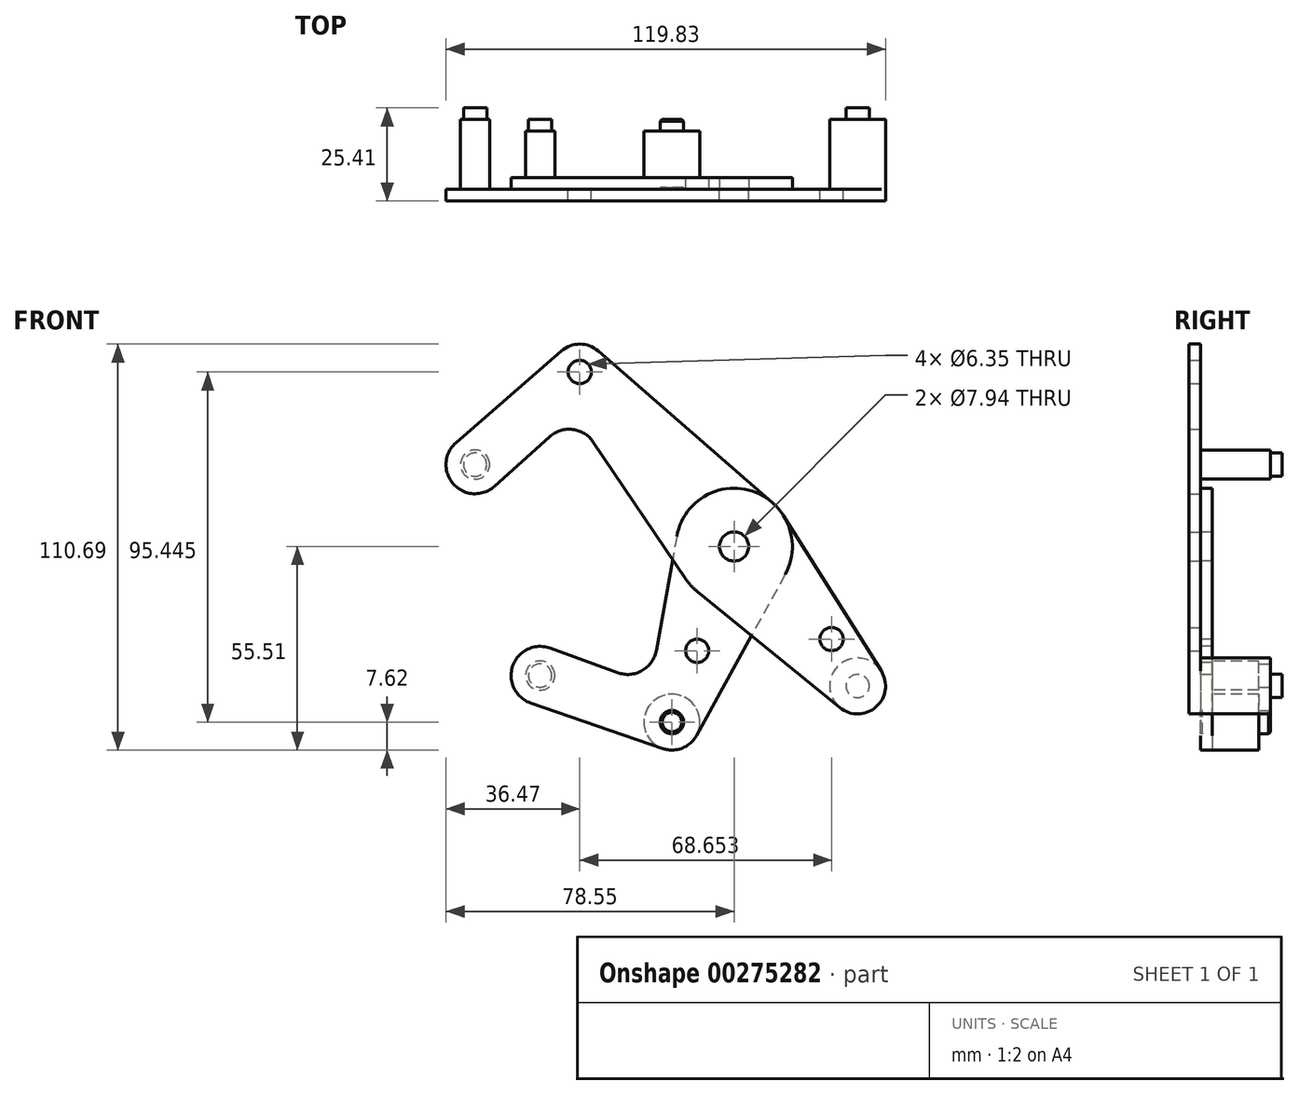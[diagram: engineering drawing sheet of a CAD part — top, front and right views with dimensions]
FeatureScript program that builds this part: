
annotation { "Feature Type Name" : "Feature", "Feature Type Description" : "" }
export const myFeature = defineFeature(function(context is Context, id is Id, definition is map)
    precondition{}
    {
        {
            var Q0;
            Q0=qCreatedBy(makeId("Front.planeOp"),FACE);
            var sketch = newSketch(context, id + "F0", { "sketchPlane" : qUnion([Q0])});
            skLineSegment(sketch, "E0", {"start": v(-42.08, 47.56) * mm, "end": v(42.08, -47.56) * mm, "construction": true});
            skCircle(sketch, "E1", {"center": v(0, 0) * mm, "radius": 3.18 * mm});
            skCircle(sketch, "E2", {"center": v(33.66, -38.04) * mm, "radius": 3.18 * mm});
            skCircle(sketch, "E3", {"center": v(-42.08, 47.56) * mm, "radius": 3.18 * mm});
            skCircle(sketch, "E4", {"center": v(-70.61, 22.3) * mm, "radius": 3.18 * mm});
            skLineSegment(sketch, "E5", {"start": v(-42.08, 47.56) * mm, "end": v(-70.61, 22.3) * mm, "construction": true});
            skCircle(sketch, "E6", {"center": v(33.66, -38.04) * mm, "radius": 7.62 * mm});
            skCircle(sketch, "E7", {"center": v(-70.61, 22.3) * mm, "radius": 7.94 * mm});
            skCircle(sketch, "E8", {"center": v(-42.08, 47.56) * mm, "radius": 7.62 * mm});
            skLineSegment(sketch, "E9", {"start": v(-75.82, 28.3) * mm, "end": v(-47.08, 53.3) * mm});
            skLineSegment(sketch, "E10", {"start": v(-65.3, 16.4) * mm, "end": v(-50.27, 29.93) * mm});
            skCircle(sketch, "E11", {"center": v(0, 0) * mm, "radius": 15.88 * mm});
            skLineSegment(sketch, "E12", {"start": v(-37.08, 53.3) * mm, "end": v(10.42, 11.98) * mm});
            skLineSegment(sketch, "E13", {"start": v(-38.39, 28.47) * mm, "end": v(-13.16, -8.89) * mm});
            skLineSegment(sketch, "E14", {"start": v(-10.02, -12.31) * mm, "end": v(28.85, -43.95) * mm});
            skLineSegment(sketch, "E15", {"start": v(13.44, 8.45) * mm, "end": v(40.12, -33.99) * mm});
            skArc(sketch, "E16.filletArc", {"start": v(-38.39, 28.47) * mm, "mid": v(-44, 31.9) * mm, "end": v(-50.27, 29.93) * mm});
            skLineSegment(sketch, "E17", {"start": v(0, 0) * mm, "end": v(-16.95, -47.89) * mm, "construction": true});
            skLineSegment(sketch, "E18", {"start": v(-16.95, -47.89) * mm, "end": v(-52.86, -35.18) * mm, "construction": true});
            skCircle(sketch, "E19", {"center": v(-52.86, -35.18) * mm, "radius": 3.18 * mm});
            skCircle(sketch, "E20", {"center": v(-16.95, -47.89) * mm, "radius": 3.18 * mm});
            skCircle(sketch, "E21", {"center": v(-52.86, -35.18) * mm, "radius": 7.94 * mm});
            skCircle(sketch, "E22", {"center": v(-16.95, -47.89) * mm, "radius": 7.62 * mm});
            skLineSegment(sketch, "E23", {"start": v(-50.15, -27.72) * mm, "end": v(-31.72, -34.42) * mm});
            skLineSegment(sketch, "E24", {"start": v(-55.45, -42.68) * mm, "end": v(-19.43, -55.1) * mm});
            skLineSegment(sketch, "E25", {"start": v(-15.63, 2.8) * mm, "end": v(-21.2, -28.35) * mm});
            skLineSegment(sketch, "E26", {"start": v(13.9, -7.66) * mm, "end": v(-10.27, -51.57) * mm});
            skArc(sketch, "E27.filletArc", {"start": v(-31.72, -34.42) * mm, "mid": v(-25.05, -33.83) * mm, "end": v(-21.2, -28.35) * mm});
            skCircle(sketch, "E28", {"center": v(-10.06, -28.43) * mm, "radius": 3.18 * mm});
            skCircle(sketch, "E29", {"center": v(26.57, -25.24) * mm, "radius": 3.18 * mm});
            skLineSegment(sketch, "E30", {"start": v(26.57, -25.24) * mm, "end": v(24.2, -27.34) * mm, "construction": true});
            skCircle(sketch, "E31", {"center": v(0, 0) * mm, "radius": 3.97 * mm});
            skSolve(sketch);
        }
        {
            var Q0;
            Q0=qCreatedBy(makeId("Front.planeOp"),FACE);
            cPlane(context, id + "F1", {"entities" : qUnion([Q0]), "cplaneType" : CPlaneType.OFFSET, "offset" : 9.52 * mm, "oppositeDirection" : true, "width" : 254 * mm, "height" : 254 * mm});
        }
        {
            var Q0;
            Q0=makeQuery(id+"F0.imprint","IMPRINT",FACE,{"disambiguationData":[TD([[makeQuery(id+"F0.imprint","IMPRINT",EDGE,{"derivedFrom":sQuery(id+"F0.wireOp",EDGE,"E2")}),-1.0]])]});
            var Q1;
            Q1=makeQuery(id+"F0.imprint","IMPRINT",FACE,{"disambiguationData":[TD([[makeQuery(id+"F0.imprint","IMPRINT",EDGE,{"derivedFrom":sQuery(id+"F0.wireOp",EDGE,"E3")}),-1.0]])]});
            var Q2;
            Q2=makeQuery(id+"F0.imprint","IMPRINT",FACE,{"disambiguationData":[TD([[makeQuery(id+"F0.imprint","IMPRINT",EDGE,{"derivedFrom":sQuery(id+"F0.wireOp",EDGE,"E4")}),-1.0]])]});
            var Q3;
            {var subQ0=sQuery(id+"F0.wireOp",EDGE,"E13");var subQ1=sQuery(id+"F0.wireOp",EDGE,"E11");var subQ2=makeQuery(id+"F0.imprint","INTERSECT",VERTEX,{"derivedFrom":[subQ1,subQ0]});Q3=makeQuery(id+"F0.imprint","IMPRINT",FACE,{"disambiguationData":[TD([[makeQuery(id+"F0.imprint","IMPRINT",EDGE,{"disambiguationData":[TD([[subQ2,1.0]])],"derivedFrom":subQ1}),-1.0]])]});}
            var Q4;
            {var subQ0=sQuery(id+"F0.wireOp",EDGE,"E14");var subQ1=sQuery(id+"F0.wireOp",EDGE,"E11");var subQ2=makeQuery(id+"F0.imprint","INTERSECT",VERTEX,{"derivedFrom":[subQ1,subQ0]});Q4=makeQuery(id+"F0.imprint","IMPRINT",FACE,{"disambiguationData":[TD([[makeQuery(id+"F0.imprint","IMPRINT",EDGE,{"disambiguationData":[TD([[subQ2,-1.0]])],"derivedFrom":subQ1}),-1.0]])]});}
            var Q5;
            {var subQ0=sQuery(id+"F0.wireOp",EDGE,"E15");Q5=makeQuery(id+"F0.imprint","IMPRINT",FACE,{"disambiguationData":[TD([[makeQuery(id+"F0.imprint","IMPRINT",EDGE,{"derivedFrom":subQ0}),-1.0]])]});}
            var Q6;
            {var subQ1=sQuery(id+"F0.wireOp",EDGE,"E9");Q6=makeQuery(id+"F0.imprint","IMPRINT",FACE,{"disambiguationData":[TD([[makeQuery(id+"F0.imprint","IMPRINT",EDGE,{"derivedFrom":subQ1}),-1.0]])]});}
            var Q7;
            Q7=makeQuery(id+"F0.imprint","IMPRINT",FACE,{"disambiguationData":[TD([[makeQuery(id+"F0.imprint","IMPRINT",EDGE,{"derivedFrom":sQuery(id+"F0.wireOp",EDGE,"E31")}),-1.0]])]});
            extrude(context, id + "F2", {"entities" : qUnion([Q0, Q1, Q2, Q3, Q4, Q5, Q6, Q7]), "depth" : 3.17 * mm});
        }
        {
            var Q0;
            Q0=makeQuery(id+"F0.imprint","IMPRINT",FACE,{"disambiguationData":[TD([[makeQuery(id+"F0.imprint","IMPRINT",EDGE,{"derivedFrom":sQuery(id+"F0.wireOp",EDGE,"E19")}),-1.0]])]});
            var Q1;
            Q1=makeQuery(id+"F0.imprint","IMPRINT",FACE,{"disambiguationData":[TD([[makeQuery(id+"F0.imprint","IMPRINT",EDGE,{"derivedFrom":sQuery(id+"F0.wireOp",EDGE,"E20")}),-1.0]])]});
            var Q2;
            {var subQ0=sQuery(id+"F0.wireOp",EDGE,"E13");var subQ1=sQuery(id+"F0.wireOp",EDGE,"E11");var subQ2=makeQuery(id+"F0.imprint","INTERSECT",VERTEX,{"derivedFrom":[subQ1,subQ0]});Q2=makeQuery(id+"F0.imprint","IMPRINT",FACE,{"disambiguationData":[TD([[makeQuery(id+"F0.imprint","IMPRINT",EDGE,{"disambiguationData":[TD([[subQ2,1.0]])],"derivedFrom":subQ1}),-1.0]])]});}
            var Q3;
            {var subQ0=sQuery(id+"F0.wireOp",EDGE,"E14");var subQ1=sQuery(id+"F0.wireOp",EDGE,"E11");var subQ2=makeQuery(id+"F0.imprint","INTERSECT",VERTEX,{"derivedFrom":[subQ1,subQ0]});Q3=makeQuery(id+"F0.imprint","IMPRINT",FACE,{"disambiguationData":[TD([[makeQuery(id+"F0.imprint","IMPRINT",EDGE,{"disambiguationData":[TD([[subQ2,-1.0]])],"derivedFrom":subQ1}),-1.0]])]});}
            var Q4;
            {var subQ10=sQuery(id+"F0.wireOp",EDGE,"E23");Q4=makeQuery(id+"F0.imprint","IMPRINT",FACE,{"disambiguationData":[TD([[makeQuery(id+"F0.imprint","IMPRINT",EDGE,{"derivedFrom":subQ10}),-1.0]])]});}
            var Q5;
            Q5=makeQuery(id+"F0.imprint","IMPRINT",FACE,{"disambiguationData":[TD([[makeQuery(id+"F0.imprint","IMPRINT",EDGE,{"derivedFrom":sQuery(id+"F0.wireOp",EDGE,"E31")}),-1.0]])]});
            var Q6;
            Q6 = qSketchRegion(id + "F4", true);
            extrude(context, id + "F3", {"entities" : qUnion([Q0, Q1, Q2, Q3, Q4, Q5, Q6]), "oppositeDirection" : true, "depth" : 3.17 * mm});
        }
        {
            var Q0;
            Q0=makeQuery(id+"F2.opExtrude","CAP_FACE",FACE,{"disambiguationData":[OSD([sQuery(id+"F0.wireOp",EDGE,"E2"),sQuery(id+"F0.wireOp",EDGE,"E3"),sQuery(id+"F0.wireOp",EDGE,"E4"),sQuery(id+"F0.wireOp",EDGE,"E6"),sQuery(id+"F0.wireOp",EDGE,"E7"),sQuery(id+"F0.wireOp",EDGE,"E8"),sQuery(id+"F0.wireOp",EDGE,"E9"),sQuery(id+"F0.wireOp",EDGE,"E10"),sQuery(id+"F0.wireOp",EDGE,"E11"),sQuery(id+"F0.wireOp",EDGE,"E12"),sQuery(id+"F0.wireOp",EDGE,"E13"),sQuery(id+"F0.wireOp",EDGE,"E14"),sQuery(id+"F0.wireOp",EDGE,"E15"),sQuery(id+"F0.wireOp",EDGE,"E16.filletArc"),sQuery(id+"F0.wireOp",EDGE,"E29"),sQuery(id+"F0.wireOp",EDGE,"E31")])],"isStart":false});
            var sketch = newSketch(context, id + "F4", { "sketchPlane" : qUnion([Q0])});
            skCircle(sketch, "E32", {"center": v(33.66, -38.04) * mm, "radius": 7.62 * mm});
            skCircle(sketch, "E33", {"center": v(-70.61, 22.3) * mm, "radius": 3.98 * mm});
            skSolve(sketch);
        }
        {
            var Q0;
            Q0=makeQuery(id+"F3.opExtrude","CAP_FACE",FACE,{"disambiguationData":[OSD([sQuery(id+"F0.wireOp",EDGE,"E11"),sQuery(id+"F0.wireOp",EDGE,"E19"),sQuery(id+"F0.wireOp",EDGE,"E20"),sQuery(id+"F0.wireOp",EDGE,"E21"),sQuery(id+"F0.wireOp",EDGE,"E22"),sQuery(id+"F0.wireOp",EDGE,"E23"),sQuery(id+"F0.wireOp",EDGE,"E24"),sQuery(id+"F0.wireOp",EDGE,"E25"),sQuery(id+"F0.wireOp",EDGE,"E26"),sQuery(id+"F0.wireOp",EDGE,"E27.filletArc"),sQuery(id+"F0.wireOp",EDGE,"E28"),sQuery(id+"F0.wireOp",EDGE,"E31")])],"isStart":true});
            var sketch = newSketch(context, id + "F5", { "sketchPlane" : qUnion([Q0])});
            skCircle(sketch, "E34", {"center": v(-16.95, -47.89) * mm, "radius": 7.62 * mm});
            skCircle(sketch, "E35", {"center": v(-52.86, -35.18) * mm, "radius": 3.98 * mm});
            skSolve(sketch);
        }
        {
            var Q0;
            Q0 = qSketchRegion(id + "F5", true);
            var Q1;
            Q1 = qSketchRegion(id + "F4", true);
            var Q2;
            Q2=sQuery(id+"F4.wireOp",EDGE,"E33");
            var Q3;
            Q3=sQuery(id+"F5.wireOp",EDGE,"E34");
            var Q4;
            Q4=sQuery(id+"F5.wireOp",EDGE,"E35");
            var Q5;
            Q5=qCreatedBy(id+"F1.planeOp",FACE);
            extrude(context, id + "F6", {"entities" : qUnion([Q0, Q1]), "surfaceEntities" : qUnion([Q2, Q3, Q4]), "endBound" : BoundingType.UP_TO_SURFACE, "oppositeDirection" : true, "endBoundEntityFace" : qUnion([Q5]), "depth" : 25.4 * mm});
        }
        {
            var Q0;
            Q0=makeQuery(id+"F3.opExtrude","SWEPT_BODY",BODY,{"disambiguationData":[OSD([sQuery(id+"F0.wireOp",EDGE,"E11"),sQuery(id+"F0.wireOp",EDGE,"E19"),sQuery(id+"F0.wireOp",EDGE,"E20"),sQuery(id+"F0.wireOp",EDGE,"E21"),sQuery(id+"F0.wireOp",EDGE,"E22"),sQuery(id+"F0.wireOp",EDGE,"E23"),sQuery(id+"F0.wireOp",EDGE,"E24"),sQuery(id+"F0.wireOp",EDGE,"E25"),sQuery(id+"F0.wireOp",EDGE,"E26"),sQuery(id+"F0.wireOp",EDGE,"E27.filletArc"),sQuery(id+"F0.wireOp",EDGE,"E28"),sQuery(id+"F0.wireOp",EDGE,"E31")])]});
            var Q1;
            Q1=makeQuery(id+"F2.opExtrude","SWEPT_BODY",BODY,{"disambiguationData":[OSD([sQuery(id+"F0.wireOp",EDGE,"E2"),sQuery(id+"F0.wireOp",EDGE,"E3"),sQuery(id+"F0.wireOp",EDGE,"E4"),sQuery(id+"F0.wireOp",EDGE,"E6"),sQuery(id+"F0.wireOp",EDGE,"E7"),sQuery(id+"F0.wireOp",EDGE,"E8"),sQuery(id+"F0.wireOp",EDGE,"E9"),sQuery(id+"F0.wireOp",EDGE,"E10"),sQuery(id+"F0.wireOp",EDGE,"E11"),sQuery(id+"F0.wireOp",EDGE,"E12"),sQuery(id+"F0.wireOp",EDGE,"E13"),sQuery(id+"F0.wireOp",EDGE,"E14"),sQuery(id+"F0.wireOp",EDGE,"E15"),sQuery(id+"F0.wireOp",EDGE,"E16.filletArc"),sQuery(id+"F0.wireOp",EDGE,"E29"),sQuery(id+"F0.wireOp",EDGE,"E31")])]});
            var Q2;
            Q2=makeQuery(id+"F6.opExtrude","SWEPT_BODY",BODY,{"disambiguationData":[OSD([sQuery(id+"F5.wireOp",EDGE,"E34")])]});
            var Q3;
            Q3=makeQuery(id+"F6.opExtrude","SWEPT_BODY",BODY,{"disambiguationData":[OSD([sQuery(id+"F5.wireOp",EDGE,"E35")])]});
            var Q4;
            Q4=makeQuery(id+"F6.opExtrude","SWEPT_BODY",BODY,{"disambiguationData":[OSD([sQuery(id+"F4.wireOp",EDGE,"E33")])]});
            var Q5;
            Q5=makeQuery(id+"F6.opExtrude","SWEPT_BODY",BODY,{"disambiguationData":[OSD([sQuery(id+"F4.wireOp",EDGE,"E32")])]});
            booleanBodies(context, id + "F7", {"operationType" : BooleanOperationType.SUBTRACTION, "tools" : qUnion([Q0, Q1]), "targets" : qUnion([Q2, Q3, Q4, Q5]), "keepTools" : true});
        }
        {
            var Q0;
            Q0=makeQuery(id+"F7.opBoolean","COPY",EDGE,{"derivedFrom":makeQuery(id+"F2.opExtrude","CAP_EDGE",EDGE,{"disambiguationData":[OSD([sQuery(id+"F0.wireOp",EDGE,"E2")])],"isStart":false})});
            var Q1;
            Q1=makeQuery(id+"F6.opExtrude","CAP_FACE",FACE,{"disambiguationData":[OSD([sQuery(id+"F5.wireOp",EDGE,"E34")])],"isStart":true});
            var Q2;
            Q2=makeQuery(id+"F7.opBoolean","COPY",EDGE,{"derivedFrom":makeQuery(id+"F3.opExtrude","CAP_EDGE",EDGE,{"disambiguationData":[OSD([sQuery(id+"F0.wireOp",EDGE,"E19")])],"isStart":true})});
            var Q3;
            Q3=makeQuery(id+"F7.opBoolean","COPY",EDGE,{"derivedFrom":makeQuery(id+"F2.opExtrude","CAP_EDGE",EDGE,{"disambiguationData":[OSD([sQuery(id+"F0.wireOp",EDGE,"E4")])],"isStart":false})});
            chamfer(context, id + "F8", {"entities" : qUnion([Q0, Q1, Q2, Q3]), "width" : 0.5 * mm, "tangentPropagation" : true});
        }
        {
            var Q0;
            Q0=makeQuery(id+"F6.opExtrude","SWEPT_BODY",BODY,{"disambiguationData":[OSD([sQuery(id+"F5.wireOp",EDGE,"E34")])]});
            var Q1;
            Q1=makeQuery(id+"F6.opExtrude","SWEPT_BODY",BODY,{"disambiguationData":[OSD([sQuery(id+"F4.wireOp",EDGE,"E33")])]});
            var Q2;
            Q2=makeQuery(id+"F6.opExtrude","SWEPT_BODY",BODY,{"disambiguationData":[OSD([sQuery(id+"F5.wireOp",EDGE,"E35")])]});
            var Q3;
            Q3=makeQuery(id+"F6.opExtrude","SWEPT_BODY",BODY,{"disambiguationData":[OSD([sQuery(id+"F4.wireOp",EDGE,"E32")])]});
            var Q4;
            Q4=qCreatedBy(id+"F1.planeOp",FACE);
            mirror(context, id + "F9", {"operationType" : NewBodyOperationType.ADD, "entities" : qUnion([Q0, Q1, Q2, Q3]), "mirrorPlane" : qUnion([Q4])});
        }
    });
